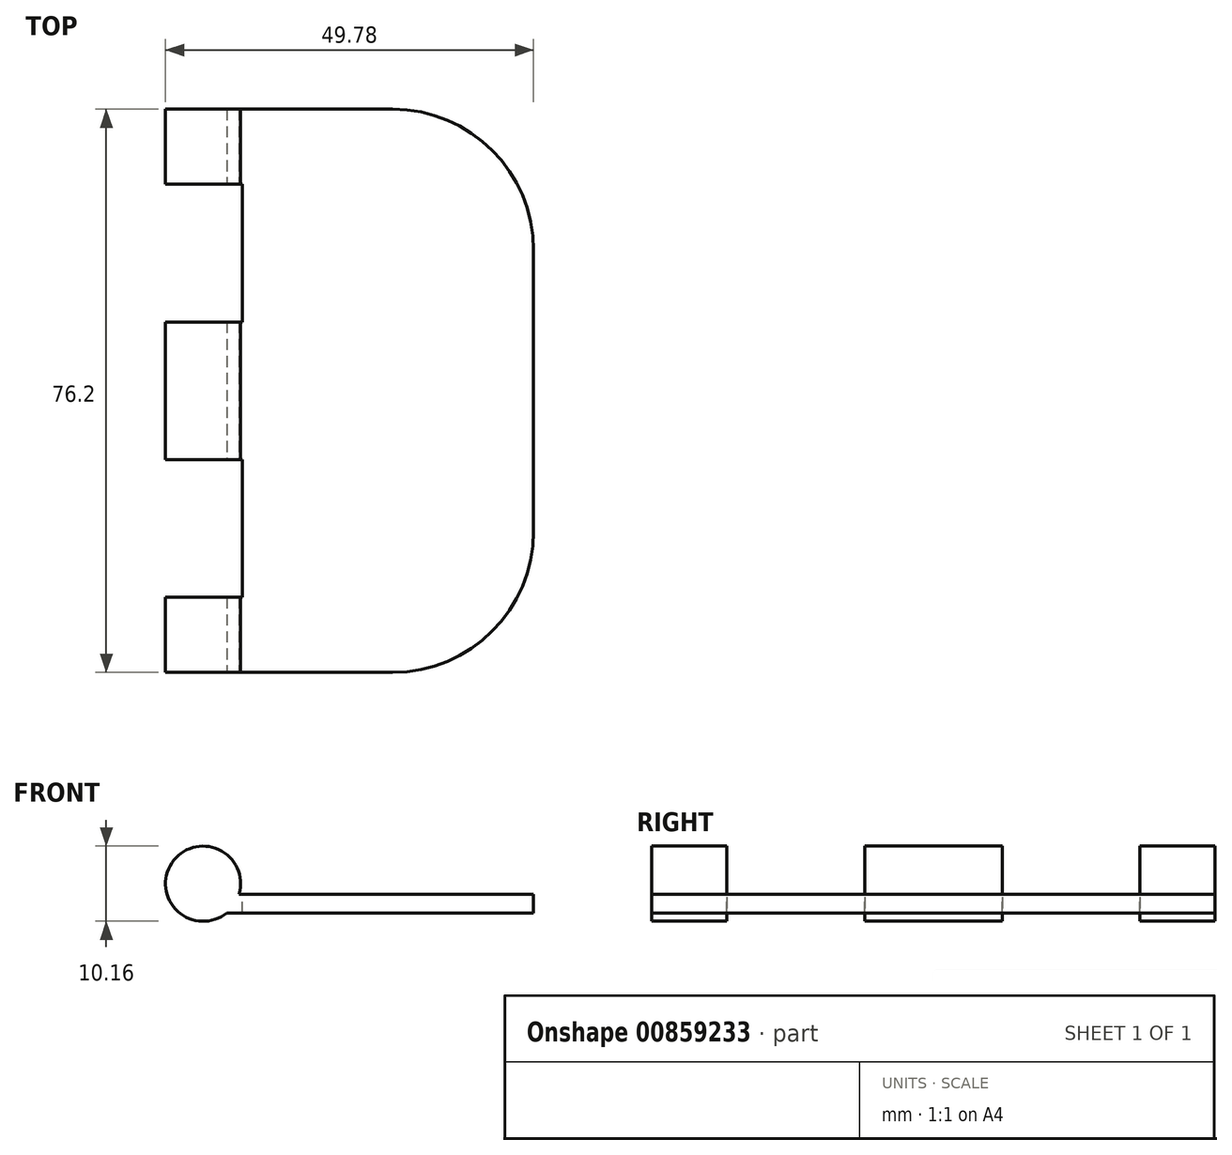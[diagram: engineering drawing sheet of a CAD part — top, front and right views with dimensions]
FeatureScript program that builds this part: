
annotation { "Feature Type Name" : "Feature", "Feature Type Description" : "" }
export const myFeature = defineFeature(function(context is Context, id is Id, definition is map)
    precondition{}
    {
        {
            var Q0;
            Q0=qCreatedBy(makeId("Top.planeOp"),FACE);
            var sketch = newSketch(context, id + "F0", { "sketchPlane" : qUnion([Q0])});
            skLineSegment(sketch, "E0.bottom", {"start": v(0, 0) * mm, "end": v(20.32, 0) * mm});
            skLineSegment(sketch, "E0.top", {"start": v(0, 76.2) * mm, "end": v(20.32, 76.2) * mm});
            skLineSegment(sketch, "E0.left", {"start": v(0, 0) * mm, "end": v(0, 76.2) * mm});
            skLineSegment(sketch, "E0.right", {"start": v(39.37, 19.05) * mm, "end": v(39.37, 57.15) * mm});
            skPoint(sketch, "E1.visualSharp", {"position": v(39.37, 0) * mm});
            skArc(sketch, "E1.filletArc", {"start": v(20.32, 0) * mm, "mid": v(33.8, 5.58) * mm, "end": v(39.37, 19.05) * mm});
            skPoint(sketch, "E2.visualSharp", {"position": v(39.37, 76.2) * mm});
            skArc(sketch, "E2.filletArc", {"start": v(39.37, 57.15) * mm, "mid": v(33.8, 70.62) * mm, "end": v(20.32, 76.2) * mm});
            skSolve(sketch);
        }
        {
            var Q0;
            Q0 = qSketchRegion(id + "F0", true);
            extrude(context, id + "F1", {"entities" : qUnion([Q0]), "depth" : 2.54 * mm, "offsetDistance" : 25.4 * mm});
        }
        {
            var Q0;
            Q0=makeQuery(id+"F1.opExtrude","SWEPT_FACE",FACE,{"disambiguationData":[OSD([sQuery(id+"F0.wireOp",EDGE,"E0.bottom")])]});
            var sketch = newSketch(context, id + "F2", { "sketchPlane" : qUnion([Q0])});
            skArc(sketch, "E3", {"start": v(-0.44, 2.54) * mm, "mid": v(-9.56, 6.75) * mm, "end": v(-2.13, 0) * mm});
            skLineSegment(sketch, "E4.bottom", {"start": v(0, 2.54) * mm, "end": v(-0.44, 2.54) * mm});
            skLineSegment(sketch, "E4.top", {"start": v(0, 0) * mm, "end": v(-2.13, 0) * mm});
            skLineSegment(sketch, "E4.left", {"start": v(0, 2.54) * mm, "end": v(0, 0) * mm});
            skPoint(sketch, "E5.orphan", {"position": v(-5.24, 0) * mm});
            skSolve(sketch);
        }
        {
            var Q0;
            Q0 = qSketchRegion(id + "F2", true);
            var Q1;
            Q1=makeQuery(id+"F1.opExtrude","SWEPT_FACE",FACE,{"disambiguationData":[OSD([sQuery(id+"F0.wireOp",EDGE,"E0.top")])]});
            extrude(context, id + "F3", {"entities" : qUnion([Q0]), "operationType" : NewBodyOperationType.ADD, "endBound" : BoundingType.UP_TO_SURFACE, "oppositeDirection" : true, "depth" : 25.4 * mm, "endBoundEntityFace" : qUnion([Q1]), "offsetDistance" : 25.4 * mm});
        }
        {
            var Q0;
            Q0=makeQuery(id+"F1.opExtrude","CAP_FACE",FACE,{"disambiguationData":[OSD([sQuery(id+"F0.wireOp",EDGE,"E0.bottom"),sQuery(id+"F0.wireOp",EDGE,"E0.top"),sQuery(id+"F0.wireOp",EDGE,"E0.left"),sQuery(id+"F0.wireOp",EDGE,"E0.right"),sQuery(id+"F0.wireOp",EDGE,"E1.filletArc"),sQuery(id+"F0.wireOp",EDGE,"E2.filletArc")])],"isStart":false});
            var sketch = newSketch(context, id + "F4", { "sketchPlane" : qUnion([Q0])});
            skLineSegment(sketch, "E6.bottom", {"start": v(-16.72, 66.04) * mm, "end": v(0, 66.04) * mm});
            skLineSegment(sketch, "E6.top", {"start": v(-16.72, 47.41) * mm, "end": v(0, 47.41) * mm});
            skLineSegment(sketch, "E6.left", {"start": v(-16.72, 66.04) * mm, "end": v(-16.72, 47.41) * mm});
            skLineSegment(sketch, "E6.right", {"start": v(0, 66.04) * mm, "end": v(0, 47.41) * mm});
            skLineSegment(sketch, "E7.bottom", {"start": v(-16.72, 28.79) * mm, "end": v(0, 28.79) * mm});
            skLineSegment(sketch, "E7.top", {"start": v(-16.72, 10.16) * mm, "end": v(0, 10.16) * mm});
            skLineSegment(sketch, "E7.left", {"start": v(-16.72, 28.79) * mm, "end": v(-16.72, 10.16) * mm});
            skLineSegment(sketch, "E7.right", {"start": v(0, 28.79) * mm, "end": v(0, 10.16) * mm});
            skLineSegment(sketch, "E8", {"start": v(-16.72, 28.79) * mm, "end": v(-16.72, 47.41) * mm});
            skSolve(sketch);
        }
        {
            var Q0;
            Q0=makeQuery(id+"F4.imprint","IMPRINT",FACE,{"disambiguationData":[TD([[makeQuery(id+"F4.imprint","IMPRINT",EDGE,{"derivedFrom":sQuery(id+"F4.wireOp",EDGE,"E6.bottom")}),-1.0]])]});
            var Q1;
            Q1=makeQuery(id+"F4.imprint","IMPRINT",FACE,{"disambiguationData":[TD([[makeQuery(id+"F4.imprint","IMPRINT",EDGE,{"derivedFrom":sQuery(id+"F4.wireOp",EDGE,"E7.bottom")}),-1.0]])]});
            extrude(context, id + "F5", {"entities" : qUnion([Q0, Q1]), "operationType" : NewBodyOperationType.REMOVE, "endBound" : BoundingType.THROUGH_ALL, "oppositeDirection" : true, "depth" : 25.4 * mm, "offsetDistance" : 25.4 * mm, "hasSecondDirection" : true, "secondDirectionBound" : SecondDirectionBoundingType.THROUGH_ALL, "secondDirectionOppositeDirection" : false, "secondDirectionDepth" : 25.4 * mm});
        }
    });
